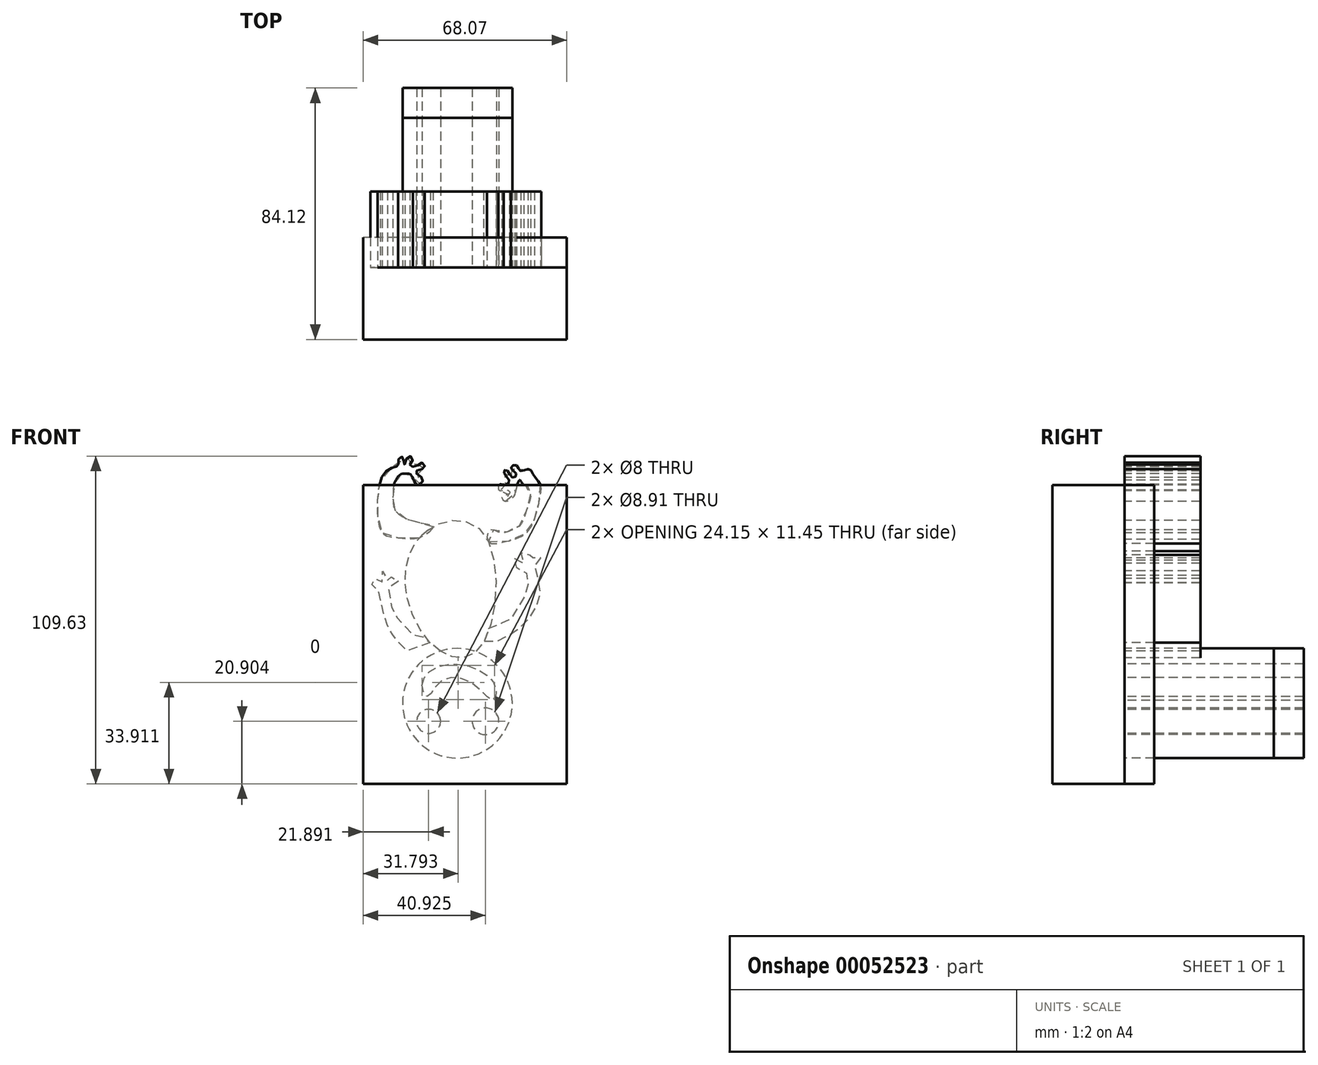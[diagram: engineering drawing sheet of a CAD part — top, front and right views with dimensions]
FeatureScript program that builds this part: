
annotation { "Feature Type Name" : "Feature", "Feature Type Description" : "" }
export const myFeature = defineFeature(function(context is Context, id is Id, definition is map)
    precondition{}
    {
        {
            var Q0;
            Q0=qCreatedBy(makeId("Top.planeOp"),FACE);
            var sketch = newSketch(context, id + "F0", { "sketchPlane" : qUnion([Q0])});
            skLineSegment(sketch, "E0", {"start": v(-25.74, 0) * mm, "end": v(-25.74, -24.12) * mm});
            skLineSegment(sketch, "E1", {"start": v(-25.74, -24.12) * mm, "end": v(42.33, -24.12) * mm});
            skLineSegment(sketch, "E2", {"start": v(42.33, -24.12) * mm, "end": v(42.33, 0) * mm});
            skLineSegment(sketch, "E3", {"start": v(42.33, 0) * mm, "end": v(-25.74, 0) * mm});
            skSolve(sketch);
        }
        {
            var Q0;
            Q0 = qSketchRegion(id + "F0", true);
            extrude(context, id + "F1", {"entities" : qUnion([Q0]), "depth" : 100 * mm});
        }
        {
            var Q0;
            Q0=makeQuery(id+"F1.opExtrude","SWEPT_FACE",FACE,{"disambiguationData":[OSD([sQuery(id+"F0.wireOp",EDGE,"E3")])]});
            var sketch = newSketch(context, id + "F2", { "sketchPlane" : qUnion([Q0])});
            skCircle(sketch, "E4", {"center": v(-5.76, 26.96) * mm, "radius": 18.34 * mm});
            skCircle(sketch, "E5", {"center": v(3.85, 20.9) * mm, "radius": 4 * mm});
            skCircle(sketch, "E6", {"center": v(-15.19, 20.9) * mm, "radius": 4.45 * mm});
            skFitSpline(sketch, "E7", {"points": [v(6.02, 33.05) * mm, v(1.5, 38.85) * mm, v(-10.65, 39.03) * mm, v(-18.63, 32.14) * mm, v(-17.72, 27.97) * mm, v(-10.81, 33.59) * mm, v(0, 34.14) * mm, v(4.21, 29.24) * mm, v(6.02, 33.05) * mm]});
            skSolve(sketch);
        }
        {
            var Q0;
            Q0 = qSketchRegion(id + "F2", true);
            extrude(context, id + "F3", {"entities" : qUnion([Q0]), "depth" : 50 * mm});
        }
        {
            var Q0;
            Q0=makeQuery(id+"F3.opExtrude","CAP_FACE",FACE,{"disambiguationData":[OSD([sQuery(id+"F2.wireOp",EDGE,"E4"),sQuery(id+"F2.wireOp",EDGE,"E5"),sQuery(id+"F2.wireOp",EDGE,"E6"),sQuery(id+"F2.wireOp",EDGE,"E7")])],"isStart":false});
            var Q1;
            Q1=makeQuery(id+"F3.boolean.opBoolean","SPLIT",FACE,{"disambiguationData":[TD([makeQuery(id+"F3.opExtrude","SWEPT_FACE",FACE,{"disambiguationData":[OSD([sQuery(id+"F2.wireOp",EDGE,"E6")])]})])],"derivedFrom":makeQuery(id+"F1.opExtrude","SWEPT_FACE",FACE,{"disambiguationData":[OSD([sQuery(id+"F0.wireOp",EDGE,"E3")])]})});
            var Q2;
            Q2=makeQuery(id+"F3.boolean.opBoolean","SPLIT",FACE,{"disambiguationData":[TD([makeQuery(id+"F3.opExtrude","SWEPT_FACE",FACE,{"disambiguationData":[OSD([sQuery(id+"F2.wireOp",EDGE,"E7")])]})])],"derivedFrom":makeQuery(id+"F1.opExtrude","SWEPT_FACE",FACE,{"disambiguationData":[OSD([sQuery(id+"F0.wireOp",EDGE,"E3")])]})});
            var Q3;
            Q3=makeQuery(id+"F3.boolean.opBoolean","SPLIT",FACE,{"disambiguationData":[TD([makeQuery(id+"F3.opExtrude","SWEPT_FACE",FACE,{"disambiguationData":[OSD([sQuery(id+"F2.wireOp",EDGE,"E5")])]})])],"derivedFrom":makeQuery(id+"F1.opExtrude","SWEPT_FACE",FACE,{"disambiguationData":[OSD([sQuery(id+"F0.wireOp",EDGE,"E3")])]})});
            extrude(context, id + "F4", {"entities" : qUnion([Q0, Q1, Q2, Q3]), "depth" : 10 * mm});
        }
        {
            var Q0;
            {var subQ1=sQuery(id+"F0.wireOp",EDGE,"E3");var subQ3=sQuery(id+"F0.wireOp",EDGE,"E0");Q0=makeQuery(id+"F3.boolean.opBoolean","SPLIT",FACE,{"disambiguationData":[TD([makeQuery(id+"F1.opExtrude","SWEPT_FACE",FACE,{"disambiguationData":[OSD([subQ3])]})])],"derivedFrom":makeQuery(id+"F1.opExtrude","SWEPT_FACE",FACE,{"disambiguationData":[OSD([subQ1])]})});}
            var sketch = newSketch(context, id + "F5", { "sketchPlane" : qUnion([Q0])});
            skFitSpline(sketch, "E8", {"points": [v(0, 44.38) * mm, v(11.65, 66.15) * mm, v(3.73, 85.24) * mm, v(-14.4, 83.93) * mm, v(-13.47, 45.7) * mm, v(0, 44.38) * mm]});
            skSolve(sketch);
        }
        {
            var Q0;
            Q0 = qSketchRegion(id + "F5", true);
            extrude(context, id + "F6", {"entities" : qUnion([Q0]), "depth" : 25.4 * mm});
        }
        {
            var Q0;
            {var subQ1=sQuery(id+"F0.wireOp",EDGE,"E3");var subQ3=sQuery(id+"F0.wireOp",EDGE,"E0");Q0=makeQuery(id+"F3.boolean.opBoolean","SPLIT",FACE,{"disambiguationData":[TD([makeQuery(id+"F1.opExtrude","SWEPT_FACE",FACE,{"disambiguationData":[OSD([subQ3])]})])],"derivedFrom":makeQuery(id+"F1.opExtrude","SWEPT_FACE",FACE,{"disambiguationData":[OSD([subQ1])]})});}
            var sketch = newSketch(context, id + "F7", { "sketchPlane" : qUnion([Q0])});
            skFitSpline(sketch, "E9", {"points": [v(-14.75, 47.68) * mm, v(-20.03, 48.1) * mm, v(-23.89, 50.4) * mm, v(-27.63, 52.97) * mm, v(-30.64, 56.6) * mm, v(-33.17, 61.93) * mm, v(-33.2, 67.34) * mm, v(-31.71, 72.92) * mm, v(-33.76, 75.25) * mm, v(-31.96, 76.52) * mm, v(-30.36, 74.74) * mm, v(-29.53, 77.32) * mm, v(-26.96, 77.2) * mm, v(-27.94, 73.81) * mm, v(-25.16, 75.5) * mm, v(-24.34, 73.4) * mm, v(-28.3, 71.2) * mm, v(-29.24, 68.32) * mm, v(-29.1, 64.43) * mm, v(-26.43, 59.9) * mm, v(-24.12, 55.72) * mm, v(-21.57, 53.86) * mm, v(-16.72, 52.42) * mm, v(-14.75, 47.68) * mm]});
            skSolve(sketch);
        }
        {
            var Q0;
            Q0 = qSketchRegion(id + "F7", true);
            extrude(context, id + "F8", {"entities" : qUnion([Q0]), "depth" : 25.4 * mm});
        }
        {
            var Q0;
            {var subQ1=sQuery(id+"F0.wireOp",EDGE,"E3");var subQ3=sQuery(id+"F0.wireOp",EDGE,"E0");Q0=makeQuery(id+"F3.boolean.opBoolean","SPLIT",FACE,{"disambiguationData":[TD([makeQuery(id+"F1.opExtrude","SWEPT_FACE",FACE,{"disambiguationData":[OSD([subQ3])]})])],"derivedFrom":makeQuery(id+"F1.opExtrude","SWEPT_FACE",FACE,{"disambiguationData":[OSD([subQ1])]})});}
            var sketch = newSketch(context, id + "F9", { "sketchPlane" : qUnion([Q0])});
            skFitSpline(sketch, "E10", {"points": [v(3.36, 47.24) * mm, v(7.79, 45.65) * mm, v(11.07, 44.52) * mm, v(13.68, 47.08) * mm, v(15.71, 49.64) * mm, v(17.52, 52.66) * mm, v(18.46, 55.4) * mm, v(19.58, 59.81) * mm, v(20.46, 63.53) * mm, v(21.1, 65.42) * mm, v(23.25, 67.18) * mm, v(22.05, 68.74) * mm, v(19.39, 67.16) * mm, v(19.92, 70.43) * mm, v(18.14, 70.85) * mm, v(17.48, 67.24) * mm, v(15.82, 69.72) * mm, v(13.97, 67.68) * mm, v(17.42, 65.34) * mm, v(16.88, 62.65) * mm, v(16.35, 59.96) * mm, v(15.7, 57.5) * mm, v(12.33, 53.29) * mm, v(10.18, 50.96) * mm, v(7.87, 49.26) * mm, v(4.85, 48.94) * mm, v(3.36, 47.24) * mm]});
            skSolve(sketch);
        }
        {
            var Q0;
            Q0 = qSketchRegion(id + "F9", true);
            extrude(context, id + "F10", {"entities" : qUnion([Q0]), "depth" : 25.4 * mm});
        }
        {
            var Q0;
            {var subQ1=sQuery(id+"F0.wireOp",EDGE,"E3");var subQ3=sQuery(id+"F0.wireOp",EDGE,"E0");Q0=makeQuery(id+"F3.boolean.opBoolean","SPLIT",FACE,{"disambiguationData":[TD([makeQuery(id+"F1.opExtrude","SWEPT_FACE",FACE,{"disambiguationData":[OSD([subQ3])]})])],"derivedFrom":makeQuery(id+"F1.opExtrude","SWEPT_FACE",FACE,{"disambiguationData":[OSD([subQ1])]})});}
            var sketch = newSketch(context, id + "F11", { "sketchPlane" : qUnion([Q0])});
            skFitSpline(sketch, "E11", {"points": [v(7.1, 82.2) * mm, v(13.68, 82.16) * mm, v(19, 83.48) * mm, v(20.72, 88.87) * mm, v(20.98, 92.71) * mm, v(20.62, 97.4) * mm, v(18.95, 103.64) * mm, v(15.21, 106) * mm, v(14.04, 106.5) * mm, v(13.92, 108.52) * mm, v(12.48, 109.32) * mm, v(11.98, 106.77) * mm, v(10.59, 109.53) * mm, v(9.18, 108.54) * mm, v(10.1, 106.57) * mm, v(8.17, 106.2) * mm, v(5.9, 107.36) * mm, v(5.25, 105.85) * mm, v(7.76, 104.8) * mm, v(7.9, 103.74) * mm, v(5.73, 101.9) * mm, v(7.43, 100) * mm, v(9.58, 103.04) * mm, v(10.68, 103.76) * mm, v(12.98, 103.58) * mm, v(14.28, 102.45) * mm, v(15.47, 100) * mm, v(15.79, 96.28) * mm, v(15.64, 93.18) * mm, v(14.78, 91.17) * mm, v(11.8, 88.87) * mm, v(8.84, 87.95) * mm, v(5.7, 87.1) * mm, v(2.45, 86.01) * mm, v(7.1, 82.2) * mm]});
            skSolve(sketch);
        }
        {
            var Q0;
            Q0 = qSketchRegion(id + "F11", true);
            extrude(context, id + "F12", {"entities" : qUnion([Q0]), "depth" : 25.4 * mm});
        }
        {
            var Q0;
            {var subQ1=sQuery(id+"F0.wireOp",EDGE,"E3");var subQ3=sQuery(id+"F0.wireOp",EDGE,"E0");Q0=makeQuery(id+"F3.boolean.opBoolean","SPLIT",FACE,{"disambiguationData":[TD([makeQuery(id+"F1.opExtrude","SWEPT_FACE",FACE,{"disambiguationData":[OSD([subQ3])]})])],"derivedFrom":makeQuery(id+"F1.opExtrude","SWEPT_FACE",FACE,{"disambiguationData":[OSD([subQ1])]})});}
            var sketch = newSketch(context, id + "F13", { "sketchPlane" : qUnion([Q0])});
            skFitSpline(sketch, "E12", {"points": [v(-16.14, 80.96) * mm, v(-21.6, 80.96) * mm, v(-26.34, 82.42) * mm, v(-29.22, 84.4) * mm, v(-30.97, 87.04) * mm, v(-32.25, 90.66) * mm, v(-33.4, 95.83) * mm, v(-33.54, 100) * mm, v(-31.33, 103.09) * mm, v(-29.67, 105.3) * mm, v(-26.73, 104.7) * mm, v(-25.38, 106.68) * mm, v(-23.66, 105.65) * mm, v(-25.5, 103.51) * mm, v(-24.17, 102.48) * mm, v(-22.18, 104.95) * mm, v(-21.28, 104.32) * mm, v(-23.1, 101.37) * mm, v(-21.85, 100) * mm, v(-19.75, 100) * mm, v(-19.79, 98.18) * mm, v(-22.8, 98.2) * mm, v(-23.02, 96.9) * mm, v(-20.73, 96.22) * mm, v(-21.51, 94.58) * mm, v(-24.21, 95.67) * mm, v(-25.14, 97.52) * mm, v(-25.02, 100) * mm, v(-25.61, 100) * mm, v(-26.6, 101.63) * mm, v(-27.88, 100) * mm, v(-28.92, 100) * mm, v(-29.78, 97.92) * mm, v(-30.24, 96.13) * mm, v(-29.2, 92.42) * mm, v(-27.57, 87.83) * mm, v(-25.9, 85.83) * mm, v(-23.94, 84.9) * mm, v(-21, 83.89) * mm, v(-18.9, 84.5) * mm, v(-16.38, 84.7) * mm, v(-16.14, 80.96) * mm]});
            skSolve(sketch);
        }
        {
            var Q0;
            Q0 = qSketchRegion(id + "F13", true);
            extrude(context, id + "F14", {"entities" : qUnion([Q0]), "depth" : 25.4 * mm});
        }
    });
